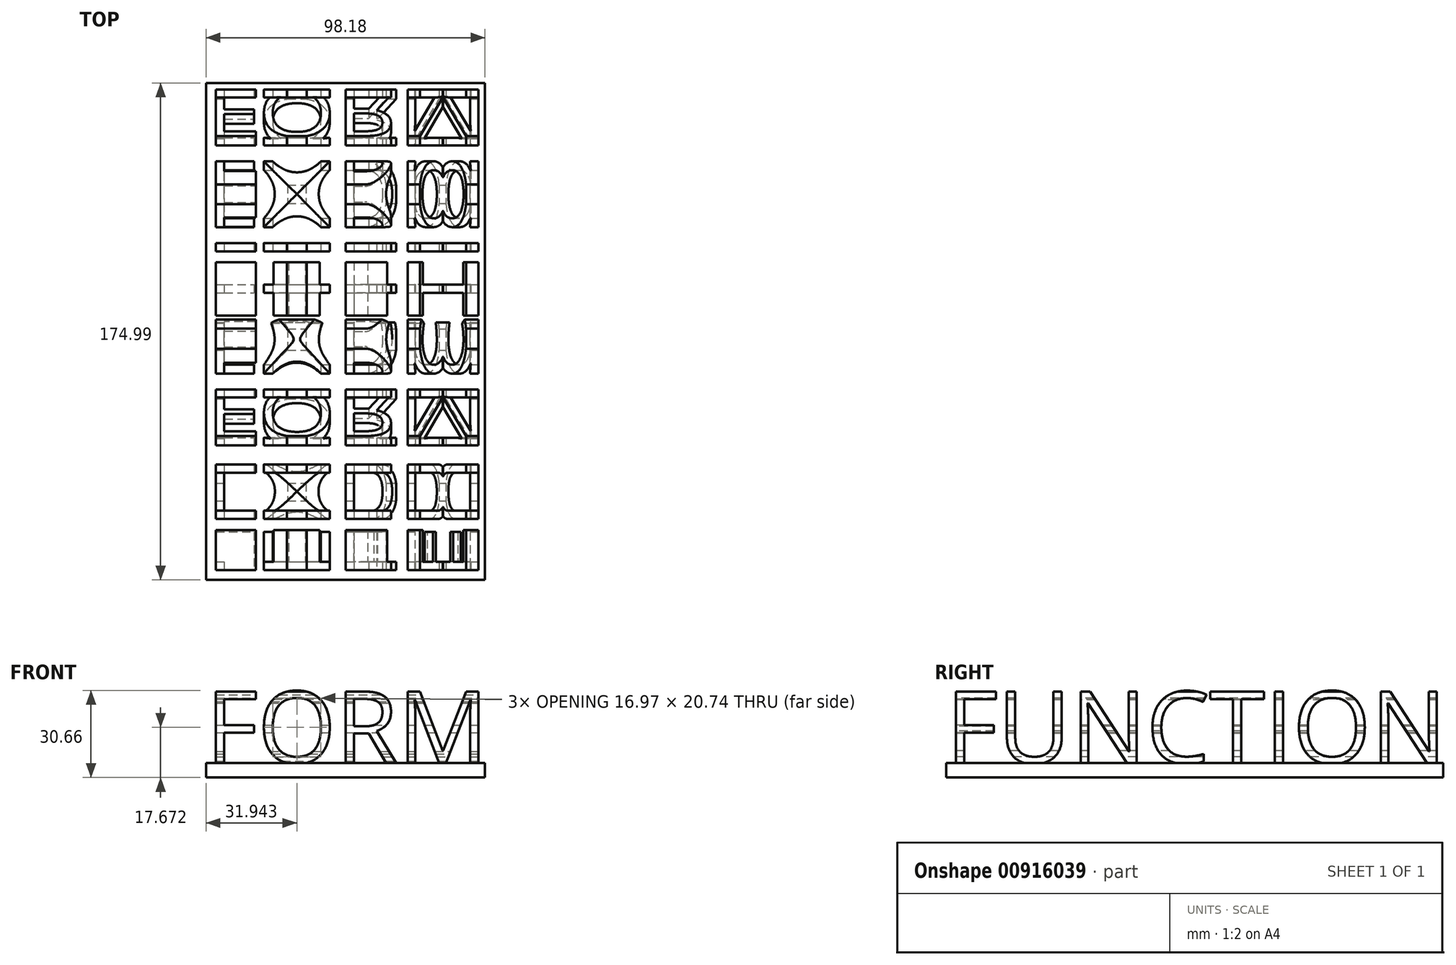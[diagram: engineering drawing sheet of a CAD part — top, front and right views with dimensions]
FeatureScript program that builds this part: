
annotation { "Feature Type Name" : "Feature", "Feature Type Description" : "" }
export const myFeature = defineFeature(function(context is Context, id is Id, definition is map)
    precondition{}
    {
        {
            var Q0;
            Q0=qCreatedBy(makeId("Front.planeOp"),FACE);
            var sketch = newSketch(context, id + "F0", { "sketchPlane" : qUnion([Q0])});
            skText(sketch, "E0", { "text": "FORM", "fontName": "OpenSans-Regular.ttf"});
            skLineSegment(sketch, "E1.bottom", {"start": v(0, 0) * mm, "end": v(98.18, 0) * mm});
            skLineSegment(sketch, "E1.top", {"start": v(0, -5.08) * mm, "end": v(98.18, -5.08) * mm});
            skLineSegment(sketch, "E1.left", {"start": v(0, 0) * mm, "end": v(0, -5.08) * mm});
            skLineSegment(sketch, "E1.right", {"start": v(98.18, 0) * mm, "end": v(98.18, -5.08) * mm});
            const initialGuessF0  = {"E0": [0, 0, 1, 0, 0.0254]};
            skSetInitialGuess(sketch, initialGuessF0);
            skSolve(sketch);
        }
        {
            var Q0;
            Q0=qCreatedBy(makeId("Right.planeOp"),FACE);
            cPlane(context, id + "F1", {"entities" : qUnion([Q0]), "cplaneType" : CPlaneType.OFFSET, "offset" : 127 * mm, "width" : 152.4 * mm, "height" : 152.4 * mm});
        }
        {
            var Q0;
            Q0=qCreatedBy(id+"F1.planeOp",FACE);
            var sketch = newSketch(context, id + "F2", { "sketchPlane" : qUnion([Q0])});
            skText(sketch, "E2", { "text": "FUNCTION", "fontName": "OpenSans-Regular.ttf"});
            skLineSegment(sketch, "E3.bottom", {"start": v(0, 0) * mm, "end": v(174.99, 0) * mm});
            skLineSegment(sketch, "E3.top", {"start": v(0, -5.08) * mm, "end": v(174.99, -5.08) * mm});
            skLineSegment(sketch, "E3.left", {"start": v(0, 0) * mm, "end": v(0, -5.08) * mm});
            skLineSegment(sketch, "E3.right", {"start": v(174.99, 0) * mm, "end": v(174.99, -5.08) * mm});
            const initialGuessF2  = {"E2": [0, 0, 1, 0, 0.0254]};
            skSetInitialGuess(sketch, initialGuessF2);
            skSolve(sketch);
        }
        {
            var Q0;
            Q0 = qSketchRegion(id + "F2", true);
            extrude(context, id + "F3", {"entities" : qUnion([Q0]), "oppositeDirection" : true, "depth" : 136.14 * mm, "offsetDistance" : 25.4 * mm});
        }
        {
            var Q0;
            Q0 = qSketchRegion(id + "F0", true);
            extrude(context, id + "F4", {"entities" : qUnion([Q0]), "oppositeDirection" : true, "depth" : 191.52 * mm, "offsetDistance" : 25.4 * mm});
        }
        {
            var Q0;
            Q0=makeQuery(id+"F3.opExtrude","SWEPT_BODY",BODY,{"disambiguationData":[OSD([sQuery(id+"F2.wireOp",EDGE,"E2.sketch_text.stroke-1"),sQuery(id+"F2.wireOp",EDGE,"E2.sketch_text.stroke-2"),sQuery(id+"F2.wireOp",EDGE,"E2.sketch_text.stroke-3"),sQuery(id+"F2.wireOp",EDGE,"E2.sketch_text.stroke-4"),sQuery(id+"F2.wireOp",EDGE,"E2.sketch_text.stroke-5"),sQuery(id+"F2.wireOp",EDGE,"E2.sketch_text.stroke-6"),sQuery(id+"F2.wireOp",EDGE,"E2.sketch_text.stroke-7"),sQuery(id+"F2.wireOp",EDGE,"E2.sketch_text.stroke-8"),sQuery(id+"F2.wireOp",EDGE,"E2.sketch_text.stroke-9"),sQuery(id+"F2.wireOp",EDGE,"E2.sketch_text.stroke-10"),sQuery(id+"F2.wireOp",EDGE,"E2.sketch_text.stroke-11"),sQuery(id+"F2.wireOp",EDGE,"E2.sketch_text.stroke-12"),sQuery(id+"F2.wireOp",EDGE,"E2.sketch_text.stroke-13"),sQuery(id+"F2.wireOp",EDGE,"E2.sketch_text.stroke-14"),sQuery(id+"F2.wireOp",EDGE,"E2.sketch_text.stroke-15"),sQuery(id+"F2.wireOp",EDGE,"E2.sketch_text.stroke-16"),sQuery(id+"F2.wireOp",EDGE,"E2.sketch_text.stroke-17"),sQuery(id+"F2.wireOp",EDGE,"E2.sketch_text.stroke-18"),sQuery(id+"F2.wireOp",EDGE,"E2.sketch_text.stroke-19"),sQuery(id+"F2.wireOp",EDGE,"E2.sketch_text.stroke-20"),sQuery(id+"F2.wireOp",EDGE,"E2.sketch_text.stroke-21"),sQuery(id+"F2.wireOp",EDGE,"E2.sketch_text.stroke-22"),sQuery(id+"F2.wireOp",EDGE,"E2.sketch_text.stroke-23"),sQuery(id+"F2.wireOp",EDGE,"E2.sketch_text.stroke-25"),sQuery(id+"F2.wireOp",EDGE,"E2.sketch_text.stroke-26"),sQuery(id+"F2.wireOp",EDGE,"E2.sketch_text.stroke-27"),sQuery(id+"F2.wireOp",EDGE,"E2.sketch_text.stroke-28"),sQuery(id+"F2.wireOp",EDGE,"E2.sketch_text.stroke-30"),sQuery(id+"F2.wireOp",EDGE,"E2.sketch_text.stroke-31"),sQuery(id+"F2.wireOp",EDGE,"E2.sketch_text.stroke-32"),sQuery(id+"F2.wireOp",EDGE,"E2.sketch_text.stroke-33"),sQuery(id+"F2.wireOp",EDGE,"E2.sketch_text.stroke-34"),sQuery(id+"F2.wireOp",EDGE,"E2.sketch_text.stroke-35"),sQuery(id+"F2.wireOp",EDGE,"E2.sketch_text.stroke-36"),sQuery(id+"F2.wireOp",EDGE,"E2.sketch_text.stroke-37"),sQuery(id+"F2.wireOp",EDGE,"E2.sketch_text.stroke-38"),sQuery(id+"F2.wireOp",EDGE,"E2.sketch_text.stroke-39"),sQuery(id+"F2.wireOp",EDGE,"E2.sketch_text.stroke-40"),sQuery(id+"F2.wireOp",EDGE,"E2.sketch_text.stroke-41"),sQuery(id+"F2.wireOp",EDGE,"E2.sketch_text.stroke-42"),sQuery(id+"F2.wireOp",EDGE,"E2.sketch_text.stroke-43"),sQuery(id+"F2.wireOp",EDGE,"E2.sketch_text.stroke-44"),sQuery(id+"F2.wireOp",EDGE,"E2.sketch_text.stroke-45"),sQuery(id+"F2.wireOp",EDGE,"E2.sketch_text.stroke-46"),sQuery(id+"F2.wireOp",EDGE,"E2.sketch_text.stroke-47"),sQuery(id+"F2.wireOp",EDGE,"E2.sketch_text.stroke-48"),sQuery(id+"F2.wireOp",EDGE,"E2.sketch_text.stroke-49"),sQuery(id+"F2.wireOp",EDGE,"E2.sketch_text.stroke-50"),sQuery(id+"F2.wireOp",EDGE,"E2.sketch_text.stroke-51"),sQuery(id+"F2.wireOp",EDGE,"E2.sketch_text.stroke-52"),sQuery(id+"F2.wireOp",EDGE,"E2.sketch_text.stroke-53"),sQuery(id+"F2.wireOp",EDGE,"E2.sketch_text.stroke-55"),sQuery(id+"F2.wireOp",EDGE,"E2.sketch_text.stroke-56"),sQuery(id+"F2.wireOp",EDGE,"E2.sketch_text.stroke-57"),sQuery(id+"F2.wireOp",EDGE,"E2.sketch_text.stroke-58"),sQuery(id+"F2.wireOp",EDGE,"E2.sketch_text.stroke-59"),sQuery(id+"F2.wireOp",EDGE,"E2.sketch_text.stroke-60"),sQuery(id+"F2.wireOp",EDGE,"E2.sketch_text.stroke-61"),sQuery(id+"F2.wireOp",EDGE,"E2.sketch_text.stroke-62"),sQuery(id+"F2.wireOp",EDGE,"E2.sketch_text.stroke-63"),sQuery(id+"F2.wireOp",EDGE,"E2.sketch_text.stroke-64"),sQuery(id+"F2.wireOp",EDGE,"E2.sketch_text.stroke-66"),sQuery(id+"F2.wireOp",EDGE,"E2.sketch_text.stroke-67"),sQuery(id+"F2.wireOp",EDGE,"E2.sketch_text.stroke-68"),sQuery(id+"F2.wireOp",EDGE,"E2.sketch_text.stroke-69"),sQuery(id+"F2.wireOp",EDGE,"E2.sketch_text.stroke-70"),sQuery(id+"F2.wireOp",EDGE,"E2.sketch_text.stroke-71"),sQuery(id+"F2.wireOp",EDGE,"E2.sketch_text.stroke-72"),sQuery(id+"F2.wireOp",EDGE,"E2.sketch_text.stroke-73"),sQuery(id+"F2.wireOp",EDGE,"E2.sketch_text.stroke-74"),sQuery(id+"F2.wireOp",EDGE,"E2.sketch_text.stroke-75"),sQuery(id+"F2.wireOp",EDGE,"E2.sketch_text.stroke-76"),sQuery(id+"F2.wireOp",EDGE,"E2.sketch_text.stroke-77"),sQuery(id+"F2.wireOp",EDGE,"E2.sketch_text.stroke-78"),sQuery(id+"F2.wireOp",EDGE,"E2.sketch_text.stroke-79"),sQuery(id+"F2.wireOp",EDGE,"E2.sketch_text.stroke-80"),sQuery(id+"F2.wireOp",EDGE,"E2.sketch_text.stroke-81"),sQuery(id+"F2.wireOp",EDGE,"E2.sketch_text.stroke-83"),sQuery(id+"F2.wireOp",EDGE,"E2.sketch_text.stroke-84"),sQuery(id+"F2.wireOp",EDGE,"E2.sketch_text.stroke-85"),sQuery(id+"F2.wireOp",EDGE,"E2.sketch_text.stroke-86"),sQuery(id+"F2.wireOp",EDGE,"E2.sketch_text.stroke-88"),sQuery(id+"F2.wireOp",EDGE,"E2.sketch_text.stroke-89"),sQuery(id+"F2.wireOp",EDGE,"E2.sketch_text.stroke-90"),sQuery(id+"F2.wireOp",EDGE,"E2.sketch_text.stroke-91"),sQuery(id+"F2.wireOp",EDGE,"E2.sketch_text.stroke-92"),sQuery(id+"F2.wireOp",EDGE,"E2.sketch_text.stroke-93"),sQuery(id+"F2.wireOp",EDGE,"E2.sketch_text.stroke-94"),sQuery(id+"F2.wireOp",EDGE,"E2.sketch_text.stroke-95"),sQuery(id+"F2.wireOp",EDGE,"E2.sketch_text.stroke-96"),sQuery(id+"F2.wireOp",EDGE,"E3.bottom"),sQuery(id+"F2.wireOp",EDGE,"E3.top"),sQuery(id+"F2.wireOp",EDGE,"E3.left"),sQuery(id+"F2.wireOp",EDGE,"E3.right")])]});
            var Q1;
            Q1=makeQuery(id+"F4.opExtrude","SWEPT_BODY",BODY,{"disambiguationData":[OSD([sQuery(id+"F0.wireOp",EDGE,"E0.sketch_text.stroke-1"),sQuery(id+"F0.wireOp",EDGE,"E0.sketch_text.stroke-2"),sQuery(id+"F0.wireOp",EDGE,"E0.sketch_text.stroke-3"),sQuery(id+"F0.wireOp",EDGE,"E0.sketch_text.stroke-4"),sQuery(id+"F0.wireOp",EDGE,"E0.sketch_text.stroke-5"),sQuery(id+"F0.wireOp",EDGE,"E0.sketch_text.stroke-6"),sQuery(id+"F0.wireOp",EDGE,"E0.sketch_text.stroke-7"),sQuery(id+"F0.wireOp",EDGE,"E0.sketch_text.stroke-8"),sQuery(id+"F0.wireOp",EDGE,"E0.sketch_text.stroke-9"),sQuery(id+"F0.wireOp",EDGE,"E0.sketch_text.stroke-10"),sQuery(id+"F0.wireOp",EDGE,"E0.sketch_text.stroke-11"),sQuery(id+"F0.wireOp",EDGE,"E0.sketch_text.stroke-12"),sQuery(id+"F0.wireOp",EDGE,"E0.sketch_text.stroke-13"),sQuery(id+"F0.wireOp",EDGE,"E0.sketch_text.stroke-14"),sQuery(id+"F0.wireOp",EDGE,"E0.sketch_text.stroke-15"),sQuery(id+"F0.wireOp",EDGE,"E0.sketch_text.stroke-16"),sQuery(id+"F0.wireOp",EDGE,"E0.sketch_text.stroke-17"),sQuery(id+"F0.wireOp",EDGE,"E0.sketch_text.stroke-18"),sQuery(id+"F0.wireOp",EDGE,"E0.sketch_text.stroke-19"),sQuery(id+"F0.wireOp",EDGE,"E0.sketch_text.stroke-20"),sQuery(id+"F0.wireOp",EDGE,"E0.sketch_text.stroke-21"),sQuery(id+"F0.wireOp",EDGE,"E0.sketch_text.stroke-22"),sQuery(id+"F0.wireOp",EDGE,"E0.sketch_text.stroke-23"),sQuery(id+"F0.wireOp",EDGE,"E0.sketch_text.stroke-24"),sQuery(id+"F0.wireOp",EDGE,"E0.sketch_text.stroke-25"),sQuery(id+"F0.wireOp",EDGE,"E0.sketch_text.stroke-26"),sQuery(id+"F0.wireOp",EDGE,"E0.sketch_text.stroke-28"),sQuery(id+"F0.wireOp",EDGE,"E0.sketch_text.stroke-29"),sQuery(id+"F0.wireOp",EDGE,"E0.sketch_text.stroke-30"),sQuery(id+"F0.wireOp",EDGE,"E0.sketch_text.stroke-31"),sQuery(id+"F0.wireOp",EDGE,"E0.sketch_text.stroke-32"),sQuery(id+"F0.wireOp",EDGE,"E0.sketch_text.stroke-33"),sQuery(id+"F0.wireOp",EDGE,"E0.sketch_text.stroke-35"),sQuery(id+"F0.wireOp",EDGE,"E0.sketch_text.stroke-36"),sQuery(id+"F0.wireOp",EDGE,"E0.sketch_text.stroke-37"),sQuery(id+"F0.wireOp",EDGE,"E0.sketch_text.stroke-38"),sQuery(id+"F0.wireOp",EDGE,"E0.sketch_text.stroke-39"),sQuery(id+"F0.wireOp",EDGE,"E0.sketch_text.stroke-40"),sQuery(id+"F0.wireOp",EDGE,"E0.sketch_text.stroke-41"),sQuery(id+"F0.wireOp",EDGE,"E0.sketch_text.stroke-42"),sQuery(id+"F0.wireOp",EDGE,"E0.sketch_text.stroke-43"),sQuery(id+"F0.wireOp",EDGE,"E0.sketch_text.stroke-44"),sQuery(id+"F0.wireOp",EDGE,"E0.sketch_text.stroke-45"),sQuery(id+"F0.wireOp",EDGE,"E0.sketch_text.stroke-46"),sQuery(id+"F0.wireOp",EDGE,"E0.sketch_text.stroke-47"),sQuery(id+"F0.wireOp",EDGE,"E0.sketch_text.stroke-49"),sQuery(id+"F0.wireOp",EDGE,"E0.sketch_text.stroke-50"),sQuery(id+"F0.wireOp",EDGE,"E0.sketch_text.stroke-51"),sQuery(id+"F0.wireOp",EDGE,"E0.sketch_text.stroke-52"),sQuery(id+"F0.wireOp",EDGE,"E0.sketch_text.stroke-53"),sQuery(id+"F0.wireOp",EDGE,"E0.sketch_text.stroke-54"),sQuery(id+"F0.wireOp",EDGE,"E0.sketch_text.stroke-55"),sQuery(id+"F0.wireOp",EDGE,"E0.sketch_text.stroke-57"),sQuery(id+"F0.wireOp",EDGE,"E0.sketch_text.stroke-58"),sQuery(id+"F0.wireOp",EDGE,"E0.sketch_text.stroke-59"),sQuery(id+"F0.wireOp",EDGE,"E0.sketch_text.stroke-60"),sQuery(id+"F0.wireOp",EDGE,"E1.bottom"),sQuery(id+"F0.wireOp",EDGE,"E1.top"),sQuery(id+"F0.wireOp",EDGE,"E1.left"),sQuery(id+"F0.wireOp",EDGE,"E1.right")])]});
            booleanBodies(context, id + "F5", {"operationType" : BooleanOperationType.INTERSECTION, "tools" : qUnion([Q0, Q1])});
        }
    });
